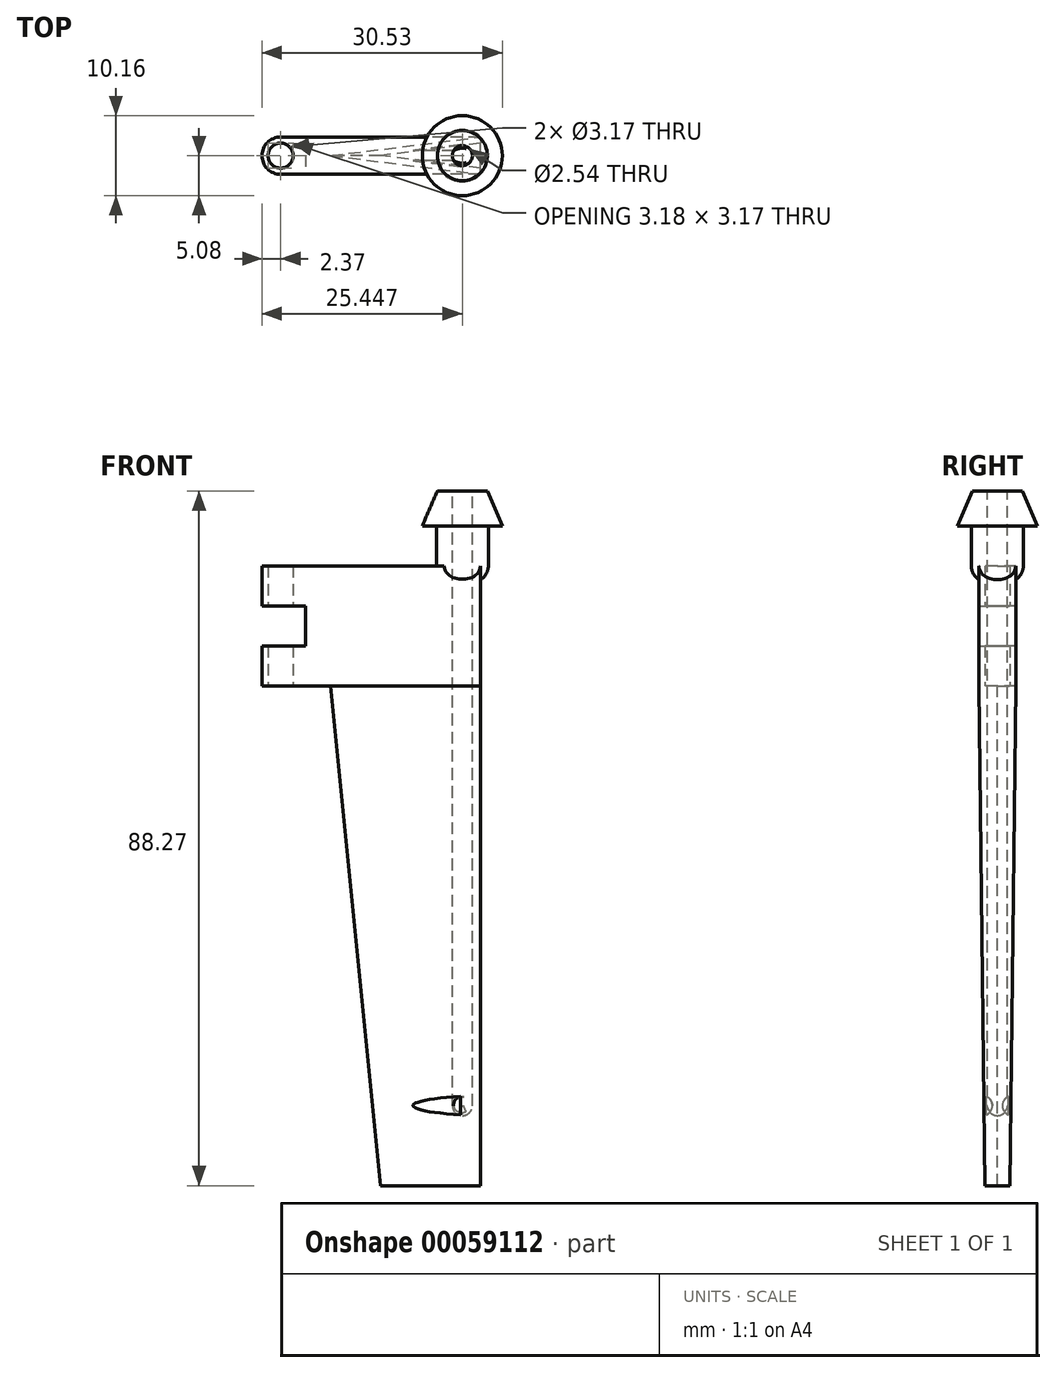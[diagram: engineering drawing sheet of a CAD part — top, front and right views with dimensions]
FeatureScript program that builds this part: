
annotation { "Feature Type Name" : "Feature", "Feature Type Description" : "" }
export const myFeature = defineFeature(function(context is Context, id is Id, definition is map)
    precondition{}
    {
        {
            var Q0;
            Q0=qCreatedBy(makeId("Front.planeOp"),FACE);
            var sketch = newSketch(context, id + "F0", { "sketchPlane" : qUnion([Q0])});
            skLineSegment(sketch, "E0", {"start": v(0, 0) * mm, "end": v(-19.05, 0) * mm});
            skLineSegment(sketch, "E1", {"start": v(-19.05, 0) * mm, "end": v(-12.7, -63.5) * mm});
            skLineSegment(sketch, "E2", {"start": v(-12.7, -63.5) * mm, "end": v(0, -63.5) * mm});
            skLineSegment(sketch, "E3", {"start": v(0, -63.5) * mm, "end": v(0, 0) * mm});
            skSolve(sketch);
        }
        {
            var Q0;
            Q0 = qSketchRegion(id + "F0", true);
            extrude(context, id + "F1", {"entities" : qUnion([Q0]), "endBound" : BoundingType.SYMMETRIC, "depth" : 4.76 * mm});
        }
        {
            var Q0;
            Q0=makeQuery(id+"F1.opExtrude","CAP_EDGE",EDGE,{"disambiguationData":[OSD([sQuery(id+"F0.wireOp",EDGE,"E1")])],"isStart":false});
            var Q1;
            Q1=makeQuery(id+"F1.opExtrude","CAP_EDGE",EDGE,{"disambiguationData":[OSD([sQuery(id+"F0.wireOp",EDGE,"E1")])],"isStart":true});
            chamfer(context, id + "F2", {"entities" : qUnion([Q0, Q1]), "chamferType" : ChamferType.TWO_OFFSETS, "width1" : 2.38 * mm, "oppositeDirection" : true, "width2" : 19.05 * mm, "tangentPropagation" : true});
        }
        {
            var Q0;
            Q0=makeQuery(id+"F1.opExtrude","SWEPT_FACE",FACE,{"disambiguationData":[OSD([sQuery(id+"F0.wireOp",EDGE,"E0")])]});
            var sketch = newSketch(context, id + "F3", { "sketchPlane" : qUnion([Q0])});
            skLineSegment(sketch, "E4.bottom", {"start": v(0, 2.37) * mm, "end": v(-25.4, 2.37) * mm});
            skLineSegment(sketch, "E4.top", {"start": v(0, -2.37) * mm, "end": v(-25.4, -2.37) * mm});
            skLineSegment(sketch, "E4.left", {"start": v(0, 2.37) * mm, "end": v(0, -2.37) * mm});
            skArc(sketch, "E5", {"start": v(-25.4, 2.37) * mm, "mid": v(-27.77, 0) * mm, "end": v(-25.4, -2.37) * mm});
            skCircle(sketch, "E6", {"center": v(-25.4, 0) * mm, "radius": 1.59 * mm});
            skSolve(sketch);
        }
        {
            var Q0;
            Q0 = qSketchRegion(id + "F3", true);
            extrude(context, id + "F4", {"entities" : qUnion([Q0]), "operationType" : NewBodyOperationType.ADD, "depth" : 15.24 * mm});
        }
        {
            var Q0;
            Q0=makeQuery(id+"F4.opExtrude","SWEPT_FACE",FACE,{"disambiguationData":[OSD([sQuery(id+"F3.wireOp",EDGE,"E4.top")])]});
            var sketch = newSketch(context, id + "F5", { "sketchPlane" : qUnion([Q0])});
            skLineSegment(sketch, "E7.bottom", {"start": v(-28.58, 10.16) * mm, "end": v(-22.23, 10.16) * mm});
            skLineSegment(sketch, "E7.top", {"start": v(-28.58, 5.08) * mm, "end": v(-22.23, 5.08) * mm});
            skLineSegment(sketch, "E7.left", {"start": v(-28.58, 10.16) * mm, "end": v(-28.58, 5.08) * mm});
            skLineSegment(sketch, "E7.right", {"start": v(-22.23, 10.16) * mm, "end": v(-22.23, 5.08) * mm});
            skPoint(sketch, "E8", {"position": v(-28.58, 7.62) * mm});
            skPoint(sketch, "E9", {"position": v(-25.4, 7.62) * mm});
            skLineSegment(sketch, "E10", {"start": v(-25.4, 7.62) * mm, "end": v(-28.58, 7.62) * mm, "construction": true});
            skSolve(sketch);
        }
        {
            var Q0;
            Q0 = qSketchRegion(id + "F5", true);
            extrude(context, id + "F6", {"entities" : qUnion([Q0]), "operationType" : NewBodyOperationType.REMOVE, "endBound" : BoundingType.THROUGH_ALL, "oppositeDirection" : true, "depth" : 25.4 * mm});
        }
        {
            var Q0;
            Q0=makeQuery(id+"F4.opExtrude","CAP_FACE",FACE,{"disambiguationData":[OSD([sQuery(id+"F3.wireOp",EDGE,"E4.bottom"),sQuery(id+"F3.wireOp",EDGE,"E4.top"),sQuery(id+"F3.wireOp",EDGE,"E4.left"),sQuery(id+"F3.wireOp",EDGE,"E5"),sQuery(id+"F3.wireOp",EDGE,"E6")])],"isStart":false});
            var sketch = newSketch(context, id + "F7", { "sketchPlane" : qUnion([Q0])});
            skLineSegment(sketch, "E11", {"start": v(0, 0) * mm, "end": v(-25.4, 0) * mm, "construction": true});
            skCircle(sketch, "E12", {"center": v(-2.32, 0) * mm, "radius": 1.27 * mm});
            skSolve(sketch);
        }
        {
            var Q0;
            Q0 = qSketchRegion(id + "F7", true);
            extrude(context, id + "F8", {"entities" : qUnion([Q0]), "operationType" : NewBodyOperationType.REMOVE, "oppositeDirection" : true, "depth" : 69.85 * mm});
        }
        {
            var Q0;
            Q0=qCreatedBy(makeId("Right.planeOp"),FACE);
            cPlane(context, id + "F9", {"entities" : qUnion([Q0]), "cplaneType" : CPlaneType.OFFSET, "offset" : 25.4 * mm, "oppositeDirection" : true, "width" : 152.4 * mm, "height" : 152.4 * mm});
        }
        {
            var Q0;
            Q0=qCreatedBy(id+"F9.planeOp",FACE);
            var sketch = newSketch(context, id + "F10", { "sketchPlane" : qUnion([Q0])});
            skLineSegment(sketch, "E13.0", {"start": v(-2.37, 15.24) * mm, "end": v(2.37, 15.24) * mm, "construction": true});
            skLineSegment(sketch, "E14.0", {"start": v(-1.58, -63.5) * mm, "end": v(1.58, -63.5) * mm, "construction": true});
            skLineSegment(sketch, "E15.0", {"start": v(0, -63.5) * mm, "end": v(0, 0) * mm, "construction": true});
            skCircle(sketch, "E16", {"center": v(-1.9, -53.34) * mm, "radius": 1.27 * mm});
            skCircle(sketch, "E17", {"center": v(1.9, -53.34) * mm, "radius": 1.27 * mm});
            skSolve(sketch);
        }
        {
            var Q0;
            Q0 = qSketchRegion(id + "F10", true);
            extrude(context, id + "F11", {"entities" : qUnion([Q0]), "operationType" : NewBodyOperationType.REMOVE, "depth" : 22.86 * mm});
        }
        {
            var Q0;
            Q0=makeQuery(id+"F8.boolean.opBoolean","COPY",EDGE,{"derivedFrom":makeQuery(id+"F8.opExtrude","CAP_EDGE",EDGE,{"disambiguationData":[OSD([sQuery(id+"F7.wireOp",EDGE,"E12")])],"isStart":false})});
            fillet(context, id + "F12", {"entities" : qUnion([Q0]), "radius" : 1.27 * mm, "tangentPropagation" : true, "allowEdgeOverflow" : false});
        }
        {
            var Q0;
            Q0=makeQuery(id+"F12.opFillet","BLEND_EDGE",EDGE,{"blendedFrom":[makeQuery(id+"F8.boolean.opBoolean","COPY",EDGE,{"derivedFrom":makeQuery(id+"F8.opExtrude","CAP_EDGE",EDGE,{"disambiguationData":[OSD([sQuery(id+"F7.wireOp",EDGE,"E12")])],"isStart":false})}),makeQuery(id+"F11.boolean.opBoolean","COPY",FACE,{"derivedFrom":makeQuery(id+"F11.opExtrude","CAP_FACE",FACE,{"disambiguationData":[OSD([sQuery(id+"F10.wireOp",EDGE,"E16")])],"isStart":false})})],"blendedInto":[makeQuery(id+"F11.boolean.opBoolean","COPY",FACE,{"derivedFrom":makeQuery(id+"F11.opExtrude","CAP_FACE",FACE,{"disambiguationData":[OSD([sQuery(id+"F10.wireOp",EDGE,"E16")])],"isStart":false})})]});
            var Q1;
            Q1=makeQuery(id+"F12.opFillet","BLEND_EDGE",EDGE,{"blendedFrom":[makeQuery(id+"F8.boolean.opBoolean","COPY",EDGE,{"derivedFrom":makeQuery(id+"F8.opExtrude","CAP_EDGE",EDGE,{"disambiguationData":[OSD([sQuery(id+"F7.wireOp",EDGE,"E12")])],"isStart":false})}),makeQuery(id+"F11.boolean.opBoolean","COPY",FACE,{"derivedFrom":makeQuery(id+"F11.opExtrude","CAP_FACE",FACE,{"disambiguationData":[OSD([sQuery(id+"F10.wireOp",EDGE,"E17")])],"isStart":false})})],"blendedInto":[makeQuery(id+"F11.boolean.opBoolean","COPY",FACE,{"derivedFrom":makeQuery(id+"F11.opExtrude","CAP_FACE",FACE,{"disambiguationData":[OSD([sQuery(id+"F10.wireOp",EDGE,"E17")])],"isStart":false})})]});
            fillet(context, id + "F13", {"entities" : qUnion([Q0, Q1]), "radius" : 1.27 * mm, "tangentPropagation" : true, "allowEdgeOverflow" : false});
        }
        {
            var Q0;
            Q0=qCreatedBy(makeId("Front.planeOp"),FACE);
            var sketch = newSketch(context, id + "F14", { "sketchPlane" : qUnion([Q0])});
            skLineSegment(sketch, "E18.0", {"start": v(-3.6, 15.24) * mm, "end": v(-1.05, 15.24) * mm, "construction": true});
            skLineSegment(sketch, "E19", {"start": v(-2.32, 15.24) * mm, "end": v(-2.32, 30.62) * mm, "construction": true});
            skLineSegment(sketch, "E20", {"start": v(-3.6, 15.24) * mm, "end": v(-5.63, 15.24) * mm, "construction": true});
            skLineSegment(sketch, "E21", {"start": v(-5.63, 15.24) * mm, "end": v(-5.63, 20.32) * mm});
            skLineSegment(sketch, "E22", {"start": v(-5.63, 20.32) * mm, "end": v(-7.4, 20.32) * mm});
            skLineSegment(sketch, "E23", {"start": v(-7.4, 20.32) * mm, "end": v(-5.5, 24.77) * mm});
            skLineSegment(sketch, "E24", {"start": v(-5.5, 24.77) * mm, "end": v(-3.6, 24.77) * mm});
            skLineSegment(sketch, "E25", {"start": v(-3.6, 24.77) * mm, "end": v(-3.6, 13.2) * mm});
            skArc(sketch, "E26", {"start": v(-5.63, 15.24) * mm, "mid": v(-5.03, 13.8) * mm, "end": v(-3.6, 13.2) * mm});
            skSolve(sketch);
        }
        {
            var Q0;
            Q0 = qSketchRegion(id + "F14", true);
            var Q1;
            Q1=sQuery(id+"F14.wireOp",EDGE,"E19");
            revolve(context, id + "F15", {"operationType" : NewBodyOperationType.ADD, "entities" : qUnion([Q0]), "axis" : qUnion([Q1]), "revolveType" : RevolveType.FULL});
        }
    });
